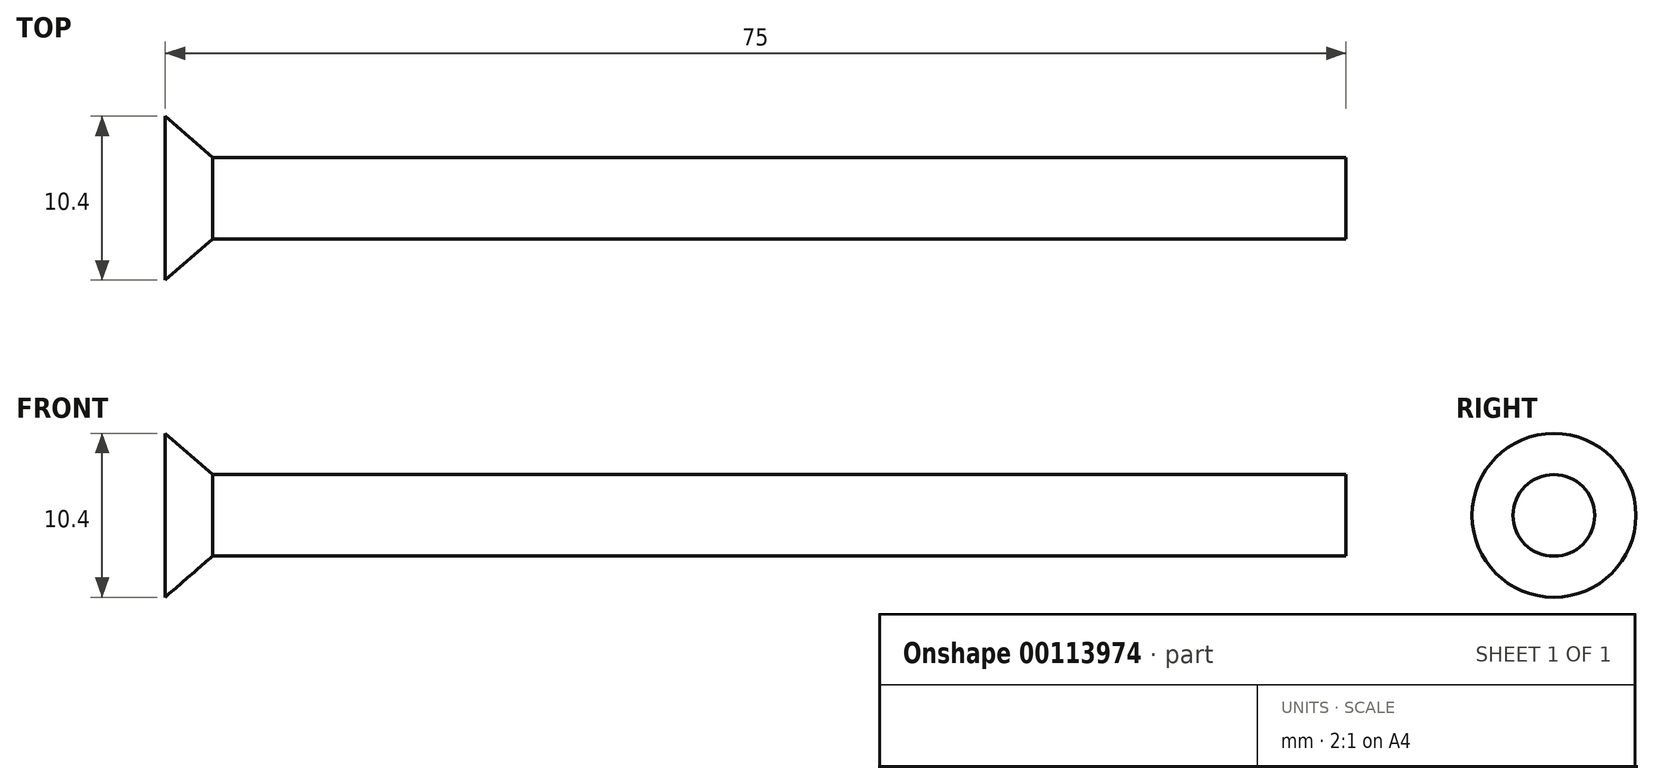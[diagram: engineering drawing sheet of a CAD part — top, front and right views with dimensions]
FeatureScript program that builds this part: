
annotation { "Feature Type Name" : "Feature", "Feature Type Description" : "" }
export const myFeature = defineFeature(function(context is Context, id is Id, definition is map)
    precondition{}
    {
        {
            var Q0;
            Q0=qCreatedBy(makeId("Front.planeOp"),FACE);
            var sketch = newSketch(context, id + "F0", { "sketchPlane" : qUnion([Q0])});
            skLineSegment(sketch, "E0", {"start": v(-37.5, 0) * mm, "end": v(-37.5, 5.2) * mm});
            skLineSegment(sketch, "E1", {"start": v(-37.5, 5.2) * mm, "end": v(-34.5, 2.6) * mm});
            skLineSegment(sketch, "E2", {"start": v(-34.5, 2.6) * mm, "end": v(37.5, 2.6) * mm});
            skLineSegment(sketch, "E3", {"start": v(37.5, 2.6) * mm, "end": v(37.5, 0) * mm});
            skLineSegment(sketch, "E4", {"start": v(37.5, 0) * mm, "end": v(-37.5, 0) * mm});
            skSolve(sketch);
        }
        {
            var Q0;
            Q0 = qSketchRegion(id + "F0", true);
            var Q1;
            Q1=sQuery(id+"F0.wireOp",EDGE,"E4");
            revolve(context, id + "F1", {"entities" : qUnion([Q0]), "axis" : qUnion([Q1]), "revolveType" : RevolveType.FULL});
        }
    });
